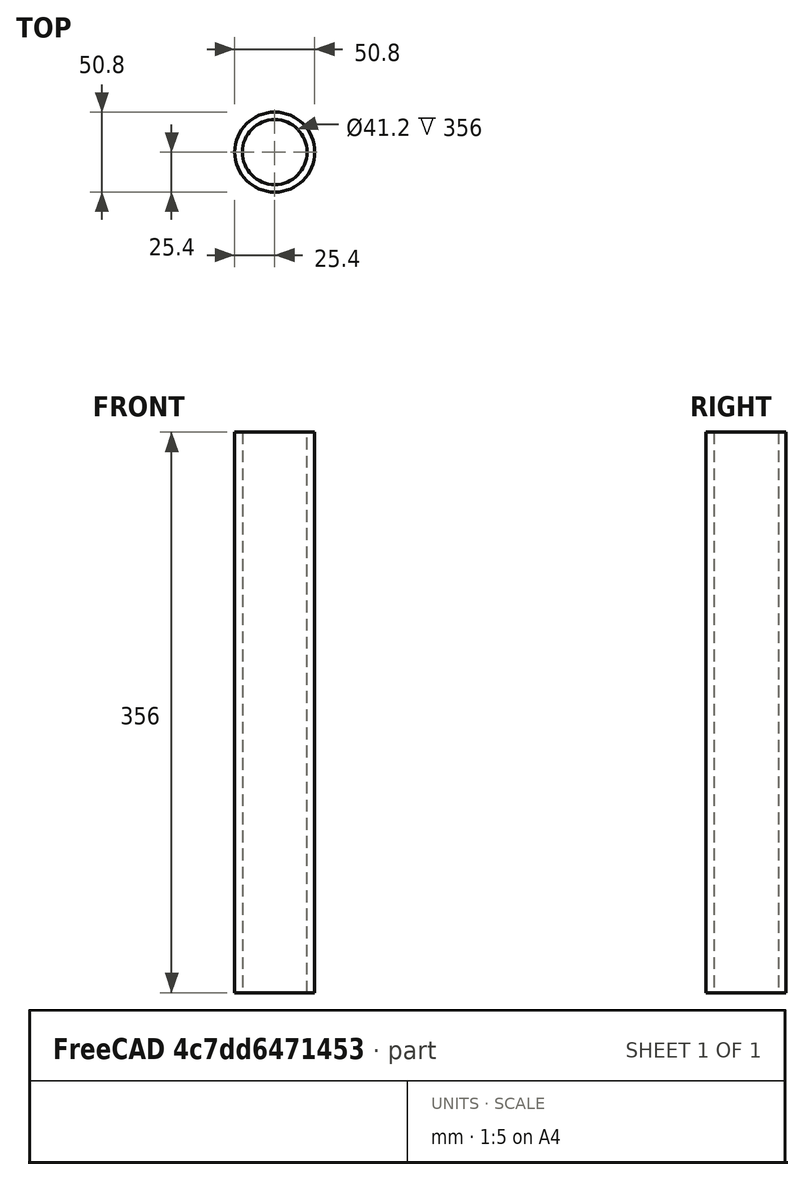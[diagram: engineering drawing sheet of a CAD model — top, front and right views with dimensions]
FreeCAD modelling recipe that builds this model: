
FCSTD DOCUMENT  (FreeCAD 0.19R24267 +99 (Git))
Label: Steel tube spacer 356mm length
License: All rights reserved
LicenseURL: http://en.wikipedia.org/wiki/All_rights_reserved
objects: Sketcher::SketchObject×1, PartDesign::Pad×1, PartDesign::Body×1
note: 4 computed .brp shape members not serialized (recipe doc carries the construction recipe); baked Part::Feature solids carry a one-line shape summary decoded from their .brp

FEATURE [Sketcher::SketchObject] Sketch  label="Cross section"
  FullyConstrained = true
  MapMode = 5
  Support = -> [XY_Plane]
  sketch-geometry (4):
    g0: Circle CenterX=0 CenterY=0 CenterZ=0 NormalX=0 NormalY=0 NormalZ=1 AngleXU=0 Radius=20.6
    g1: Circle CenterX=0 CenterY=0 CenterZ=0 NormalX=0 NormalY=0 NormalZ=1 AngleXU=0 Radius=25.4
    g2: GeomPoint X=20.6 Y=0 Z=0
    g3: GeomPoint X=25.4 Y=0 Z=0
  constraints (8):
    c: Coincident(g0,g-1)
    c: Coincident(g1,g0)
    c: PointOnObject(g2,g0)
    c: PointOnObject(g3,g1)
    c: PointOnObject(g3,g-1)
    c: PointOnObject(g2,g-1)
    c: DistanceX(g2,g3) = 4.8
    c: Diameter(g1) = 50.8
FEATURE [PartDesign::Pad] Pad  label="Length"
  Direction = (1,1,1)
  Length = 356
  Length2 = 100
  Profile = -> Sketch
  Type = 0
FEATURE [PartDesign::Body] Body
  Group = -> [Sketch,Pad]
  Origin = -> Origin
  Tip = -> Pad
